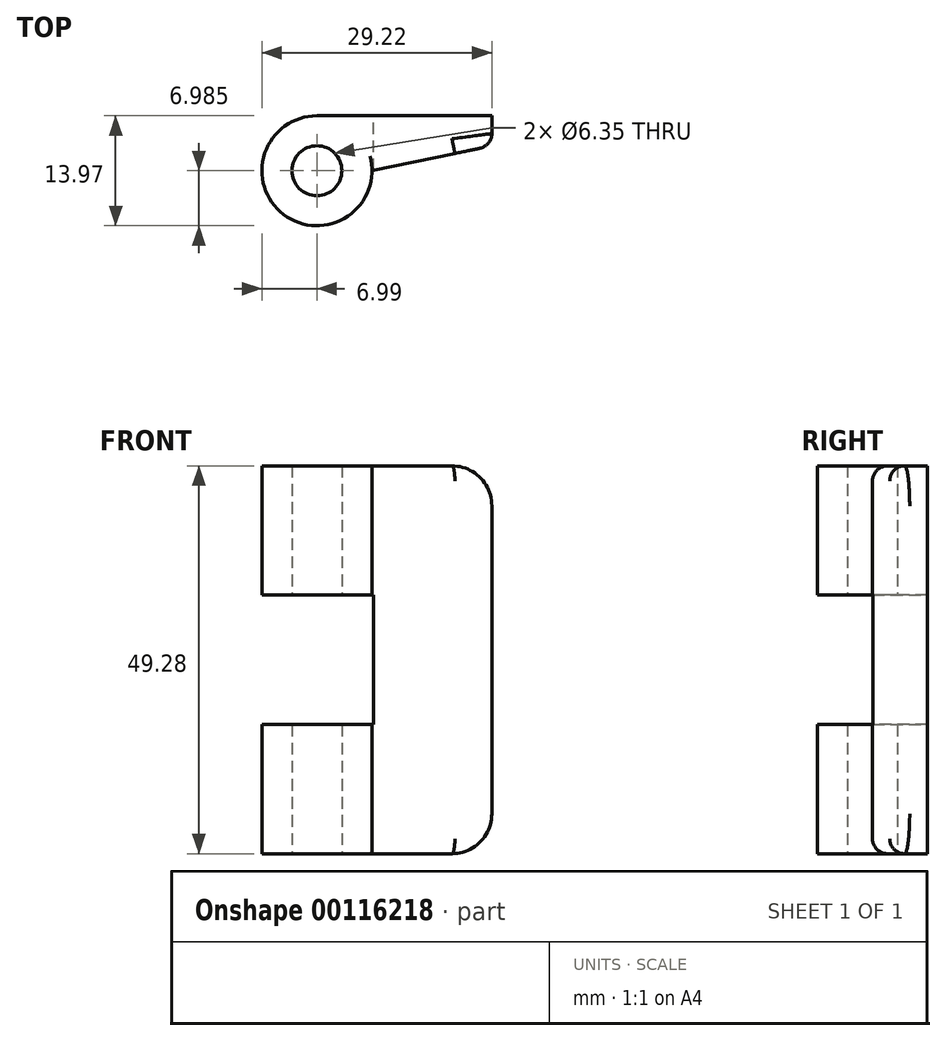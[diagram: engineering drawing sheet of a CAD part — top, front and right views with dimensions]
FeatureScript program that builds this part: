
annotation { "Feature Type Name" : "Feature", "Feature Type Description" : "" }
export const myFeature = defineFeature(function(context is Context, id is Id, definition is map)
    precondition{}
    {
        {
            var Q0;
            Q0=qCreatedBy(makeId("Top.planeOp"),FACE);
            var sketch = newSketch(context, id + "F0", { "sketchPlane" : qUnion([Q0])});
            skCircle(sketch, "E0", {"center": v(0, -6.99) * mm, "radius": 6.99 * mm});
            skLineSegment(sketch, "E1", {"start": v(0, 0) * mm, "end": v(22.23, 0) * mm});
            skLineSegment(sketch, "E2", {"start": v(22.23, 0) * mm, "end": v(22.23, -3.81) * mm});
            skLineSegment(sketch, "E3", {"start": v(22.23, -3.81) * mm, "end": v(6.99, -6.99) * mm});
            skSolve(sketch);
        }
        {
            var Q0;
            Q0 = qSketchRegion(id + "F0", true);
            extrude(context, id + "F1", {"entities" : qUnion([Q0]), "depth" : 49.28 * mm});
        }
        {
            var Q0;
            Q0=makeQuery(id+"F1.opExtrude","SWEPT_FACE",FACE,{"disambiguationData":[OSD([sQuery(id+"F0.wireOp",EDGE,"E1")])]});
            var sketch = newSketch(context, id + "F2", { "sketchPlane" : qUnion([Q0])});
            skLineSegment(sketch, "E4", {"start": v(0, 0) * mm, "end": v(0, 16.4) * mm});
            skLineSegment(sketch, "E5", {"start": v(0, 49.28) * mm, "end": v(0, 32.87) * mm});
            skLineSegment(sketch, "E6.bottom", {"start": v(8.03, 32.87) * mm, "end": v(-7.2, 32.87) * mm});
            skLineSegment(sketch, "E6.top", {"start": v(8.03, 16.4) * mm, "end": v(-7.2, 16.4) * mm});
            skLineSegment(sketch, "E6.left", {"start": v(8.03, 32.87) * mm, "end": v(8.03, 16.4) * mm});
            skLineSegment(sketch, "E6.right", {"start": v(-7.2, 32.87) * mm, "end": v(-7.2, 16.4) * mm});
            skSolve(sketch);
        }
        {
            var Q0;
            Q0 = qSketchRegion(id + "F2", true);
            extrude(context, id + "F3", {"entities" : qUnion([Q0]), "operationType" : NewBodyOperationType.REMOVE, "endBound" : BoundingType.SYMMETRIC, "oppositeDirection" : true, "depth" : 50.8 * mm});
        }
        {
            var Q0;
            Q0=makeQuery(id+"F1.opExtrude","CAP_EDGE",EDGE,{"disambiguationData":[OSD([sQuery(id+"F0.wireOp",EDGE,"E3")])],"isStart":false});
            var Q1;
            Q1=makeQuery(id+"F1.opExtrude","SWEPT_EDGE",EDGE,{"disambiguationData":[OSD([sQuery(id+"F0.wireOp",EDGE,"E2"),sQuery(id+"F0.wireOp",EDGE,"E3")])]});
            var Q2;
            Q2=makeQuery(id+"F1.opExtrude","CAP_EDGE",EDGE,{"disambiguationData":[OSD([sQuery(id+"F0.wireOp",EDGE,"E3")])],"isStart":true});
            fillet(context, id + "F4", {"entities" : qUnion([Q0, Q1, Q2]), "radius" : 1.9 * mm, "tangentPropagation" : true, "allowEdgeOverflow" : false});
        }
        {
            var Q0;
            Q0=makeQuery(id+"F1.opExtrude","CAP_FACE",FACE,{"disambiguationData":[OSD([sQuery(id+"F0.wireOp",EDGE,"E0"),sQuery(id+"F0.wireOp",EDGE,"E1"),sQuery(id+"F0.wireOp",EDGE,"E2"),sQuery(id+"F0.wireOp",EDGE,"E3")])],"isStart":true});
            var sketch = newSketch(context, id + "F5", { "sketchPlane" : qUnion([Q0])});
            skCircle(sketch, "E7", {"center": v(0, 6.99) * mm, "radius": 3.18 * mm});
            skSolve(sketch);
        }
        {
            var Q0;
            Q0 = qSketchRegion(id + "F5", true);
            extrude(context, id + "F6", {"entities" : qUnion([Q0]), "operationType" : NewBodyOperationType.REMOVE, "endBound" : BoundingType.THROUGH_ALL, "oppositeDirection" : true, "depth" : 25.4 * mm});
        }
        {
            var Q0;
            Q0=makeQuery(id+"F1.opExtrude","CAP_EDGE",EDGE,{"disambiguationData":[OSD([sQuery(id+"F0.wireOp",EDGE,"E2")])],"isStart":false});
            var Q1;
            Q1=makeQuery(id+"F1.opExtrude","CAP_EDGE",EDGE,{"disambiguationData":[OSD([sQuery(id+"F0.wireOp",EDGE,"E2")])],"isStart":true});
            fillet(context, id + "F7", {"entities" : qUnion([Q0, Q1]), "radius" : 5.08 * mm, "tangentPropagation" : true, "allowEdgeOverflow" : false});
        }
    });
